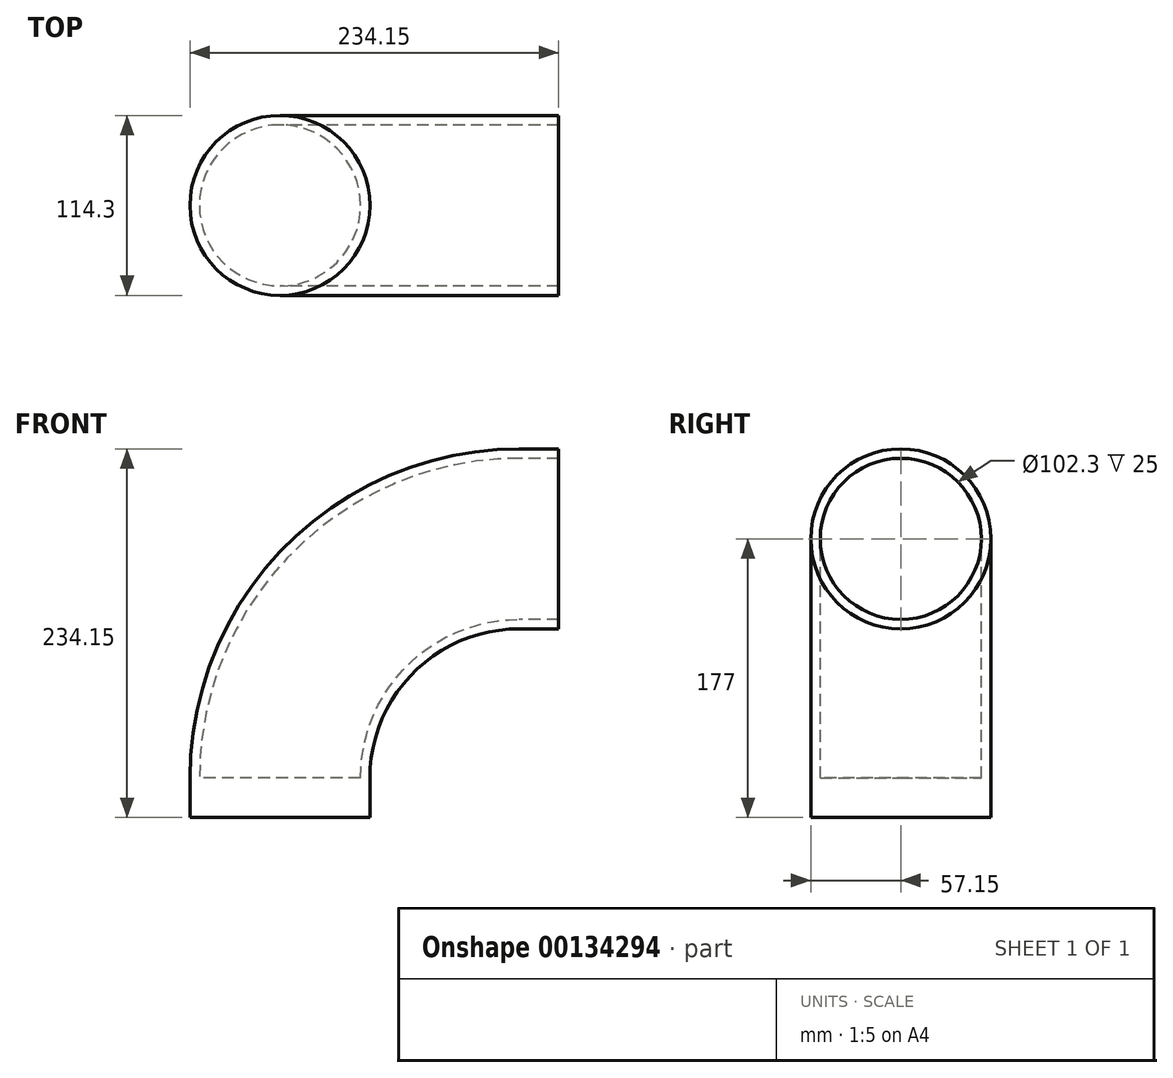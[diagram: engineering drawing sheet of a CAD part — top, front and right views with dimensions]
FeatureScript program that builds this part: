
annotation { "Feature Type Name" : "Feature", "Feature Type Description" : "" }
export const myFeature = defineFeature(function(context is Context, id is Id, definition is map)
    precondition{}
    {
        {
            var Q0;
            Q0=qCreatedBy(makeId("Top.planeOp"),FACE);
            var sketch = newSketch(context, id + "F0", { "sketchPlane" : qUnion([Q0])});
            skCircle(sketch, "E0", {"center": v(0, 0) * mm, "radius": 57.15 * mm});
            skSolve(sketch);
        }
        {
            var Q0;
            Q0=qCreatedBy(makeId("Front.planeOp"),FACE);
            var sketch = newSketch(context, id + "F1", { "sketchPlane" : qUnion([Q0])});
            skLineSegment(sketch, "E1", {"start": v(0, 0) * mm, "end": v(0, 0) * mm});
            skLineSegment(sketch, "E2", {"start": v(152, 152) * mm, "end": v(152, 152) * mm});
            skPoint(sketch, "E3.visualSharp", {"position": v(0, 152) * mm});
            skArc(sketch, "E3.filletArc", {"start": v(152, 152) * mm, "mid": v(44.52, 107.48) * mm, "end": v(0, 0) * mm});
            skSolve(sketch);
        }
        {
            var Q0;
            Q0=makeQuery(id+"F0.imprint","IMPRINT",FACE,{"disambiguationData":[TD([[makeQuery(id+"F0.imprint","IMPRINT",EDGE,{"derivedFrom":sQuery(id+"F0.wireOp",EDGE,"E0")}),1.0]])]});
            var Q1;
            Q1=sQuery(id+"F1.wireOp",EDGE,"E3.filletArc");
            sweep(context, id + "F2", {"profiles" : qUnion([Q0]), "path" : qUnion([Q1])});
        }
        {
            var Q0;
            Q0=makeQuery(id+"F2.opSweep","CAP_FACE",FACE,{"disambiguationData":[OSD([sQuery(id+"F0.wireOp",EDGE,"E0"),sQuery(id+"F1.wireOp",VERTEX,"E3.filletArc.start")])],"isStart":false});
            var Q1;
            Q1=makeQuery(id+"F2.opSweep","CAP_FACE",FACE,{"disambiguationData":[OSD([sQuery(id+"F0.wireOp",EDGE,"E0"),sQuery(id+"F1.wireOp",VERTEX,"E3.filletArc.end")])],"isStart":true});
            shell(context, id + "F3", {"entities" : qUnion([Q0, Q1]), "thickness" : 6 * mm});
        }
        {
            var Q0;
            Q0 = qSketchRegion(id + "F0", true);
            extrude(context, id + "F4", {"entities" : qUnion([Q0]), "operationType" : NewBodyOperationType.ADD, "oppositeDirection" : true, "depth" : 25 * mm});
        }
        {
            var Q0;
            Q0=makeQuery(id+"F2.opSweep","CAP_FACE",FACE,{"disambiguationData":[OSD([sQuery(id+"F0.wireOp",EDGE,"E0"),sQuery(id+"F1.wireOp",VERTEX,"E3.filletArc.start")])],"isStart":false});
            var sketch = newSketch(context, id + "F5", { "sketchPlane" : qUnion([Q0])});
            skCircle(sketch, "E4.0", {"center": v(0, 152) * mm, "radius": 57.15 * mm});
            skCircle(sketch, "E5.0", {"center": v(0, 152) * mm, "radius": 51.15 * mm});
            skSolve(sketch);
        }
        {
            var Q0;
            Q0 = qSketchRegion(id + "F5", true);
            extrude(context, id + "F6", {"entities" : qUnion([Q0]), "operationType" : NewBodyOperationType.ADD, "depth" : 25 * mm});
        }
    });
